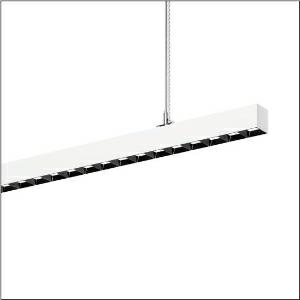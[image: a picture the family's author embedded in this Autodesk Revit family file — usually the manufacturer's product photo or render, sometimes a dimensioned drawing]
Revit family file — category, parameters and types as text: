
# Revit family: silica_r__21_51mx31tat7w_6f20
name_source: partatom
category: Lighting Fixtures
units: mm (PartAtom-declared; Revit-internal decimal feet)

## family parameters
Cut with Voids When Loaded = No
Host = Face
Light Source = No
Part Type = Normal
Room Calculation Point = No
Round Connector Dimension = Use Diameter
Shared = No

## types (1)
- --- (1 x LED, 6220 lm, 53.5 W, 6500K)
    Apparent Load = 54 VA
    CIE Flux Codes = 85 99 100 60 100
    Color Rendering = 80
    Color Temperature = 6500K
    Default Elevation = 1800 mm
    Description = Silica® 21, office luminaire, primary light control with darklight reflector, of PMMA, black, CAT 2 (L<= 3000cd/m²), light emission: direct/indirect distribution, primary light characteristic: symmetric, installation type: suspended mounting, LED, rated luminous flux: 6.220lm, luminous efficacy: 111lm/W, light colour: 8tw, colour temperature: 2700..6500K, control gear: DALI DT8, with terminal, 3+2-pole, max. 2.5mm², mains connection: 220..240V, AC, 50/60Hz, rated input power: 56.2W, luminaire housing, of aluminium, traffic white (RAL 9016), length: 1.204mm, width: 53mm, height: 53mm, protection rating (complete): IP20, insulation class (complete): insulation class I (protective earthing), certification: CE, permissible operating ambient temperature: 0..+35°C, standard: EN 50419, packaging unit: 1 piece
    Height = 53 mm
    Lamp = 1 x LED
    Lamp Light Flux = 6220 lm
    Lamp Power = 53.5 W
    Lamp count = 1
    Length = 1204 mm
    Luminous efficacy = 116 lm/W
    Manufacturer = Siteco
    ModVariant = No
    Model = 51MX31TAT7W
    Mounting Place = Ceiling
    Mounting Type = Pendant
    Number of Poles = 1
    OnlyDefault = Yes
    Power Factor = 1
    Product Name = Silica® 21
    Product group = office luminaire | ceiling pendant
    ProductGroupID = 904
    Protection Class = Protection class I
    Protection Degree = IP 20
    RLX_Detail_Level = 1
    RLX_Emergency_Light_Flux = 0 lm
    RLX_Emergency_Type = 0
    RLX_Emergency_Type_DB = No
    RlxData = <blob elided: 40469 chars, md5=79130301>
    Socket = socket
    Standby Power = 0 W
    System Light Flux = 6220 lm
    System Power = 54 W
    Type Comments = individual setting
    Type Image = l_1335871.jpg
    URL = http://relux.com
    VarID = @adj_139908
    Voltage = 0 V
    Weight = 0.00 kg
    Width = 53 mm

## geometry (parser evidence)
native form markers: Blend x4, Sweep x13
no freeform markers — native parametric forms only
